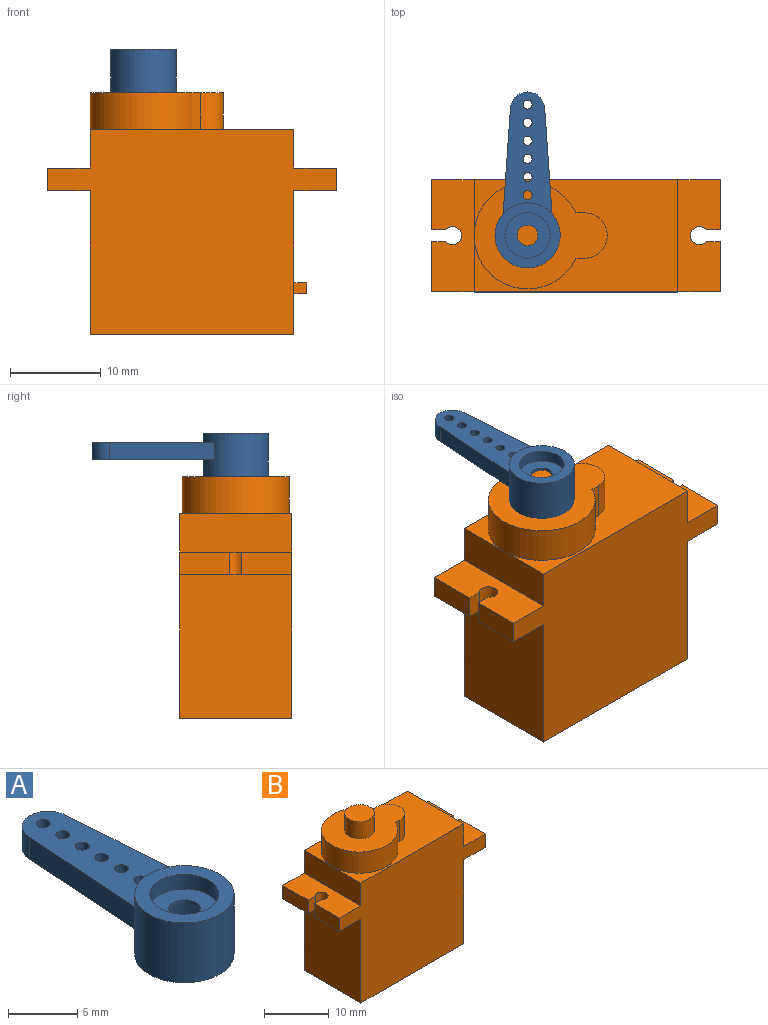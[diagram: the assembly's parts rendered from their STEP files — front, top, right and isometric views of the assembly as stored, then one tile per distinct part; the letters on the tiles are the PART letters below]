
ASSEMBLY  parts=2 mates=1
PART A: 19 faces, bbox 7.2x19.5x5.3 mm
  f0: cylinder r=3.6mm len=7.2mm, axis (0,0,-1), area 108mm2, adj f3,f4,f8,f9,f17,f18
  f1: cylinder r=2.5mm len=5mm, axis (0,0,-1), area 58.1mm2, adj f4,f7
  f2: cylinder r=2.5mm len=5mm, axis (0,0,-1), area 20.4mm2, adj f3,f6
  f3: plane 7.2x7.2mm, normal (0,0,1), area 21.1mm2, adj f0,f2
  f4: plane 7.2x7.2mm, normal (0,0,-1), area 21.1mm2, adj f0,f1
  f5: cylinder r=1.15mm len=2.3mm, axis (0,0,-1), area 2.2mm2, adj f6,f7
  f6: plane 5x5mm, normal (0,0,1), area 15.5mm2, adj f2,f5
  f7: plane 5x5mm, normal (0,0,-1), area 15.5mm2, adj f1,f5
  f8: plane 11.57x1.95mm, normal (-1,0.07,0), area 22.6mm2, adj f0,f16,f17,f18
  f9: plane 11.57x1.95mm, normal (1,0.07,0), area 22.6mm2, adj f0,f16,f17,f18
  f10: cylinder r=0.5mm len=1.95mm, axis (0,0,-1), area 6.1mm2, adj f17,f18
  f11: cylinder r=0.5mm len=1.95mm, axis (0,0,-1), area 6.1mm2, adj f17,f18
  f12: cylinder r=0.5mm len=1.95mm, axis (0,0,-1), area 6.1mm2, adj f17,f18
  f13: cylinder r=0.5mm len=1.95mm, axis (0,0,-1), area 6.1mm2, adj f17,f18
  f14: cylinder r=0.5mm len=1.95mm, axis (0,0,-1), area 6.1mm2, adj f17,f18
  f15: cylinder r=0.5mm len=1.95mm, axis (0,0,-1), area 6.1mm2, adj f17,f18
  f16: cylinder r=1.9mm len=3.8mm, axis (0,0,-1), area 11.6mm2, adj f8,f9,f17,f18
  f17: plane 13.47x5.4mm, normal (0,0,1), area 49.6mm2, adj f0,f8,f9,f10,f11,f12,f13,f14
  f18: plane 13.47x5.4mm, normal (0,0,-1), area 49.6mm2, adj f0,f8,f9,f10,f11,f12,f13,f14
PART B: 34 faces, bbox 31.9x12.4x29.9 mm
  f0: plane 5.55x2.5mm, normal (-1,0,0), area 13.9mm2, adj f2,f3,f17,f32
  f1: plane 5.55x2.5mm, normal (1,0,0), area 13.9mm2, adj f12,f14,f17,f28
  f2: plane 12.4x4.7mm, normal (0,0,1), area 53.3mm2, adj f0,f8,f9,f16,f17,f31,f32,f33
  f3: plane 12.4x4.7mm, normal (0,0,-1), area 53.3mm2, adj f0,f9,f10,f16,f17,f31,f32,f33
  f4: cylinder r=2.3mm len=4.6mm, axis (0,0,1), area 46.2mm2, adj f5,f27
  f5: plane 4.6x4.6mm, normal (0,0,1), area 16.6mm2, adj f4
  f6: plane 22.5x12.4mm, normal (0,0,1), area 156.9mm2, adj f8,f15,f16,f17,f23,f24,f25,f26
  f7: plane 15.9x12.4mm, normal (1,0,0), area 192.8mm2, adj f11,f12,f16,f17,f18,f19,f20,f21
  f8: plane 12.4x4.3mm, normal (-1,0,0), area 53.3mm2, adj f2,f6,f16,f17
  f9: plane 5.55x2.5mm, normal (-1,0,0), area 13.9mm2, adj f2,f3,f16,f33
  f10: plane 15.9x12.4mm, normal (-1,0,0), area 197.2mm2, adj f3,f11,f16,f17
  f11: plane 22.5x12.4mm, normal (0,0,-1), area 279mm2, adj f7,f10,f16,f17
  f12: plane 12.4x4.7mm, normal (0,0,-1), area 53.3mm2, adj f1,f7,f13,f16,f17,f28,f29,f30
  f13: plane 5.55x2.5mm, normal (1,0,0), area 13.9mm2, adj f12,f14,f16,f29
  f14: plane 12.4x4.7mm, normal (0,0,1), area 53.3mm2, adj f1,f13,f15,f16,f17,f28,f29,f30
  f15: plane 12.4x4.3mm, normal (1,0,0), area 53.3mm2, adj f6,f14,f16,f17
  f16: plane 31.9x22.7mm, normal (0,-1,0), area 534.2mm2, adj f2,f3,f6,f7,f8,f9,f10,f11
  f17: plane 31.9x22.7mm, normal (0,1,0), area 534.2mm2, adj f0,f1,f2,f3,f6,f7,f8,f10
  f18: plane 1.4x1.2mm, normal (0,-1,0), area 1.7mm2, adj f7,f19,f21,f22
  f19: plane 3.6x1.4mm, normal (0,0,-1), area 5mm2, adj f7,f18,f20,f22
  f20: plane 1.4x1.2mm, normal (0,1,0), area 1.7mm2, adj f7,f19,f21,f22
  f21: plane 3.6x1.4mm, normal (0,0,1), area 5mm2, adj f7,f18,f20,f22
  f22: plane 3.6x1.2mm, normal (1,0,0), area 4.3mm2, adj f18,f19,f20,f21
  f23: cylinder r=2.5mm len=5mm, axis (0,0,1), area 31.4mm2, adj f6,f24,f26,f27
  f24: plane 4x0.96mm, normal (0,1,0), area 3.8mm2, adj f6,f23,f25,f27
  f25: cylinder r=5.9mm len=11.8mm, axis (0,0,1), area 127.6mm2, adj f6,f24,f26,f27
  f26: plane 4x0.96mm, normal (0,-1,0), area 3.8mm2, adj f6,f23,f25,f27
  f27: plane 14.7x11.8mm, normal (0,0,1), area 105.5mm2, adj f4,f23,f24,f25,f26
  f28: plane 2.5x1.54mm, normal (0,-1,0), area 3.9mm2, adj f1,f12,f14,f30
  f29: plane 2.5x1.54mm, normal (0,1,0), area 3.9mm2, adj f12,f13,f14,f30
  f30: cylinder r=1mm len=2.5mm, axis (0,0,1), area 12.2mm2, adj f12,f14,f28,f29
  f31: cylinder r=1mm len=2.5mm, axis (0,0,1), area 12.2mm2, adj f2,f3,f32,f33
  f32: plane 2.5x1.54mm, normal (0,-1,0), area 3.9mm2, adj f0,f2,f3,f31
  f33: plane 2.5x1.54mm, normal (0,1,0), area 3.9mm2, adj f2,f3,f9,f31
PLACE A rot(axis=(0.04,0.78,-0.62),0deg) t=(17.48,-10.96,12.9)mm
PLACE B rot(axis=(0.04,0.78,-0.62),0deg) t=(17.48,-10.96,13.4)mm
MATE revolute A.f0 <-> B.f4  axis (0,0,-1) through (17.48,-10.96,13.4)mm
